# Revit family: Plumbing_Fixture-Grohe-Eurocube-Single_Pillar_Bidet_Mixer-12-METRIC
name_source: partatom
category: Plumbing Fixtures
revit_build: Autodesk Revit Architecture 2012 (Build: 20110916_2132(x64)
units: mm (PartAtom-declared; Revit-internal decimal feet)

## types (1)
- Eurocube_Bidet_Mixer-23138000
    ADA Compliant = Yes
    Assembly Code = C1030220
    AssetType = Fixed
    Barcode = 0
    CW Connection = No
    CWFU = 4.5
    Connection Diameter = 10 mm  [stored 0.0328084 ft]
    Cost = 0 $
    Default Elevation = 600 mm
    Description = For a sharp, tailored look in your bathroom choose Eurocube. Here is a design so cleverly engineered that we are able to offer an extensive choice featuring true square design for the basin, bidet, shower and bath. Across the range, cut-out detailing on the lever handles reduces the perceived volume of each piece, while highlighting the minimalist appeal of the collection. Perfectly aligned to the design needs of today’s cosmopolitan consumers, Eurocube offers cutting-edge, geometric styling at an unbeatable price. At the same time it benefits from two leading GROHE technologies: GROHE SilkMove® – for smooth and comfortable operation of single lever mixers and GROHE StarLight® – our resilient chrome finish.
    Ecojoy = No
    ExpectedLife = 0
    Faucet Material = Grohe-Chrome
    Flow Pressure = min 1 bar/recommended 1-5bar
    Flow Rate = 5.4L/min
    HW Connection = No
    HWFU = 4.5
    Height = 139 mm  [stored 0.456037 ft]
    Keynote = N13
    Length = 112 mm  [stored 0.367454 ft]
    Low Emitting Material = Yes
    MaintenanceInformation = http://cdn08.grohe.com
    Manufacturer = Grohe AG
    Mixed Water Radius = 5 mm  [stored 0.0164042 ft]
    Model = Eurocube Bidet mixer 23138000
    ModelNumber = Eurocube Bidet mixer 23138000
    Name = Eurocube Bidet mixer 23138000
    Operating Pressure = max 10 bar
    Percentage of Recycled Content = 0
    Product Documentation Link = http://cdn08.grohe.com
    Product Page URL = http://www.grohe.com
    SerialNumber = 0
    Spare Parts List = http://www.grohe.com
    TagNumber = 0
    Temp - Hot Water Supply = max 80 deg C
    Temp - Hot Water Supply (Recommended) = 60 deg C
    Test Pressure = 16 bar
    Type Comments = Pillar Tap, monobloc installation, metal lever, ceramic headpart
    URL = www.grohe.com
    Vent Connection = No
    WFU = 0
    Waste Connection = No
    Width = 34 mm
    _BIMspec_GUID = 0
    _current revision = 1
    _distributed by = www.bimstore.co.uk

note: [stored X ft] marks values corroborated as IEEE doubles in the binary element streams (Revit-internal decimal feet)

## geometry (parser evidence)
native form markers: Sweep x1
no freeform markers — native parametric forms only
